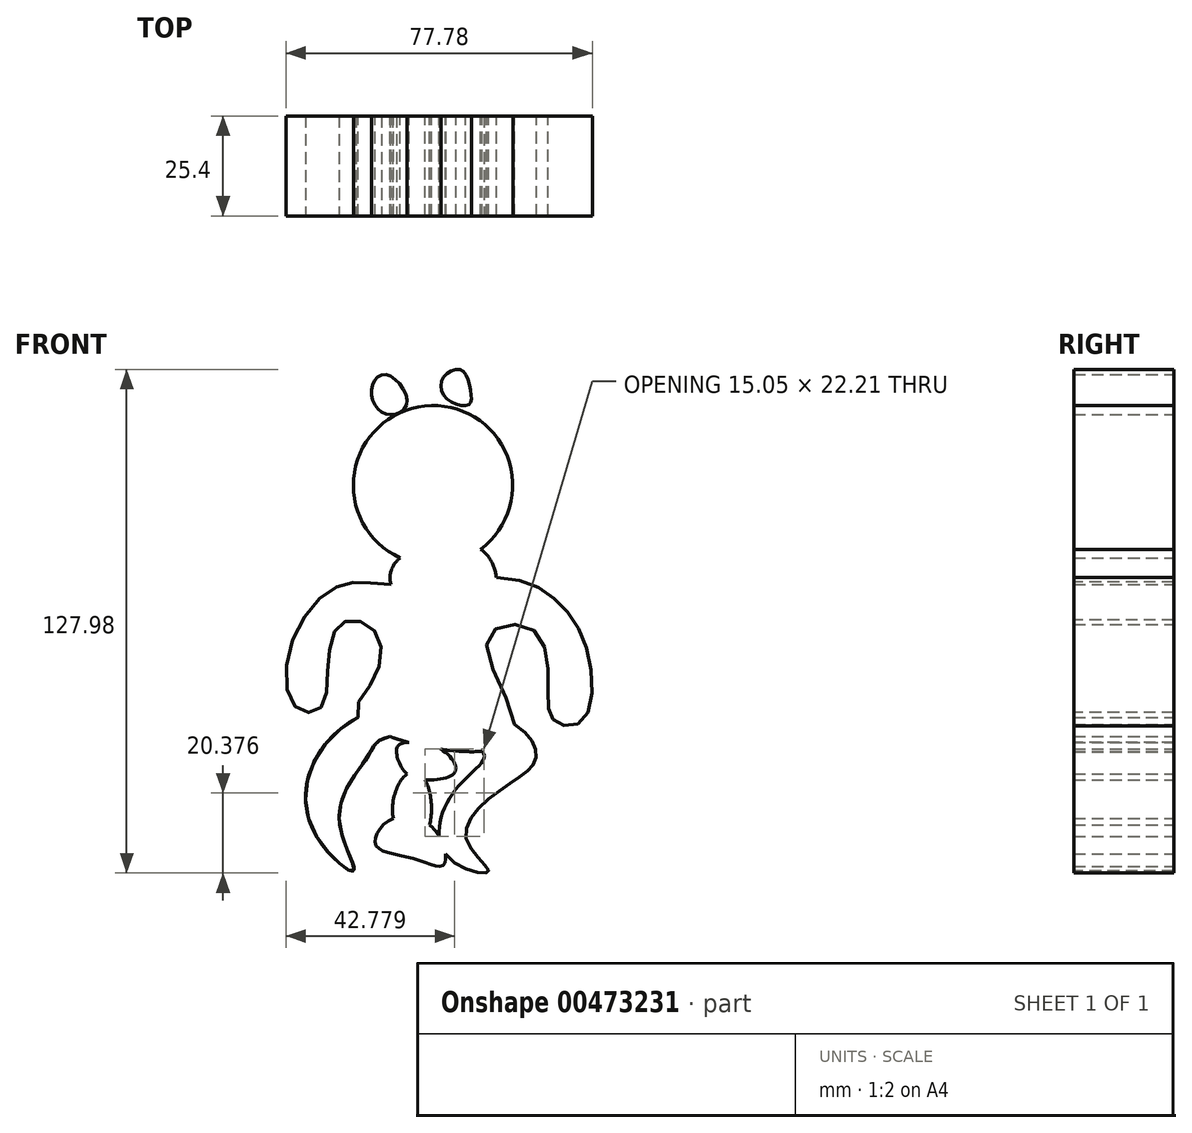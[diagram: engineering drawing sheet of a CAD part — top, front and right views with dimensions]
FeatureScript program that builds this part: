
annotation { "Feature Type Name" : "Feature", "Feature Type Description" : "" }
export const myFeature = defineFeature(function(context is Context, id is Id, definition is map)
    precondition{}
    {
        {
            var Q0;
            Q0=qCreatedBy(makeId("Front.planeOp"),FACE);
            var sketch = newSketch(context, id + "F0", { "sketchPlane" : qUnion([Q0])});
            skCircle(sketch, "E0", {"center": v(0, 25.17) * mm, "radius": 20.25 * mm});
            skSolve(sketch);
        }
        {
            var Q0;
            Q0 = qSketchRegion(id + "F0", true);
            extrude(context, id + "F1", {"entities" : qUnion([Q0]), "depth" : 25.4 * mm});
        }
        {
            var Q0;
            Q0=qCreatedBy(makeId("Front.planeOp"),FACE);
            var sketch = newSketch(context, id + "F2", { "sketchPlane" : qUnion([Q0])});
            skFitSpline(sketch, "E1", {"points": [v(-11.9, 43.27) * mm, v(-15.67, 49.13) * mm, v(-11.98, 53.29) * mm, v(-6.63, 46.06) * mm, v(-11.9, 43.27) * mm]});
            skSolve(sketch);
        }
        {
            var Q0;
            Q0 = qSketchRegion(id + "F2", true);
            extrude(context, id + "F3", {"entities" : qUnion([Q0]), "depth" : 25.4 * mm});
        }
        {
            var Q0;
            Q0=qCreatedBy(makeId("Front.planeOp"),FACE);
            var sketch = newSketch(context, id + "F4", { "sketchPlane" : qUnion([Q0])});
            skFitSpline(sketch, "E2", {"points": [v(3.54, 47.13) * mm, v(2.52, 52.42) * mm, v(7.2, 54.42) * mm, v(9.6, 48.75) * mm, v(9.04, 45.6) * mm, v(3.54, 47.13) * mm]});
            skSolve(sketch);
        }
        {
            var Q0;
            Q0 = qSketchRegion(id + "F4", true);
            extrude(context, id + "F5", {"entities" : qUnion([Q0]), "depth" : 25.4 * mm});
        }
        {
            var Q0;
            Q0=qCreatedBy(makeId("Front.planeOp"),FACE);
            var sketch = newSketch(context, id + "F6", { "sketchPlane" : qUnion([Q0])});
            skFitSpline(sketch, "E3", {"points": [v(-8.62, 6.56) * mm, v(-8.62, -3.04) * mm, v(13.51, -5.2) * mm, v(12.34, 8.72) * mm, v(-8.62, 6.56) * mm]});
            skSolve(sketch);
        }
        {
            var Q0;
            Q0 = qSketchRegion(id + "F6", true);
            extrude(context, id + "F7", {"entities" : qUnion([Q0]), "operationType" : NewBodyOperationType.ADD, "depth" : 25.4 * mm});
        }
        {
            var Q0;
            Q0=qCreatedBy(makeId("Front.planeOp"),FACE);
            var sketch = newSketch(context, id + "F8", { "sketchPlane" : qUnion([Q0])});
            skFitSpline(sketch, "E4", {"points": [v(-10.97, 0) * mm, v(-22.92, 0) * mm, v(-35.06, -12.63) * mm, v(-35.26, -30.85) * mm, v(-28.8, -31.63) * mm, v(-26.64, -19.3) * mm, v(-22.52, -9.5) * mm, v(-14.5, -12.24) * mm, v(-15.28, -24.38) * mm, v(-18.6, -34.37) * mm, v(19.98, -39.66) * mm, v(13.71, -14.2) * mm, v(25.46, -11.65) * mm, v(29.18, -28.1) * mm, v(31.14, -34.96) * mm, v(37.8, -34.77) * mm, v(39.76, -19.3) * mm, v(32.12, -4.8) * mm, v(17.63, 1.66) * mm, v(-10.97, 0) * mm]});
            skSolve(sketch);
        }
        {
            var Q0;
            Q0 = qSketchRegion(id + "F8", true);
            extrude(context, id + "F9", {"entities" : qUnion([Q0]), "operationType" : NewBodyOperationType.ADD, "depth" : 25.4 * mm});
        }
        {
            var Q0;
            Q0=qCreatedBy(makeId("Front.planeOp"),FACE);
            var sketch = newSketch(context, id + "F10", { "sketchPlane" : qUnion([Q0])});
            skFitSpline(sketch, "E5", {"points": [v(-19.4, -33.98) * mm, v(-31.34, -60.42) * mm, v(-20.17, -72.76) * mm, v(-23.9, -59.25) * mm, v(-16.45, -43.58) * mm, v(-11.75, -38.88) * mm, v(12.73, -42.8) * mm, v(5.68, -52.2) * mm, v(3.72, -69.24) * mm, v(14.1, -72.96) * mm, v(8.42, -64.73) * mm, v(17.43, -52) * mm, v(26.05, -44.56) * mm, v(20.37, -35.35) * mm, v(-19.4, -33.98) * mm]});
            skSolve(sketch);
        }
        {
            var Q0;
            Q0 = qSketchRegion(id + "F10", true);
            extrude(context, id + "F11", {"entities" : qUnion([Q0]), "operationType" : NewBodyOperationType.ADD, "depth" : 25.4 * mm});
        }
        {
            var Q0;
            Q0=qCreatedBy(makeId("Front.planeOp"),FACE);
            var sketch = newSketch(context, id + "F12", { "sketchPlane" : qUnion([Q0])});
            skFitSpline(sketch, "E6", {"points": [v(-5.1, -40.25) * mm, v(-9, -41.23) * mm, v(-7.25, -47.5) * mm, v(0, -49.65) * mm, v(5.68, -47.5) * mm, v(2.74, -42.4) * mm, v(-5.1, -40.25) * mm]});
            skSolve(sketch);
        }
        {
            var Q0;
            Q0 = qSketchRegion(id + "F12", true);
            extrude(context, id + "F13", {"entities" : qUnion([Q0]), "operationType" : NewBodyOperationType.ADD, "depth" : 25.4 * mm});
        }
        {
            var Q0;
            Q0=qCreatedBy(makeId("Front.planeOp"),FACE);
            var sketch = newSketch(context, id + "F14", { "sketchPlane" : qUnion([Q0])});
            skFitSpline(sketch, "E7", {"points": [v(-6.46, -48.08) * mm, v(-9.8, -60.23) * mm, v(-2.55, -63.75) * mm, v(-1.76, -50.24) * mm, v(-6.46, -48.08) * mm]});
            skSolve(sketch);
        }
        {
            var Q0;
            Q0=makeQuery(id+"F14.imprint","IMPRINT",FACE,{"disambiguationData":[TD([[makeQuery(id+"F14.imprint","IMPRINT",EDGE,{"derivedFrom":sQuery(id+"F14.wireOp",EDGE,"E7")}),1.0]])]});
            extrude(context, id + "F15", {"entities" : qUnion([Q0]), "operationType" : NewBodyOperationType.ADD, "depth" : 25.4 * mm});
        }
        {
            var Q0;
            Q0=qCreatedBy(makeId("Front.planeOp"),FACE);
            var sketch = newSketch(context, id + "F16", { "sketchPlane" : qUnion([Q0])});
            skFitSpline(sketch, "E8", {"points": [v(-11.16, -60.03) * mm, v(-14.5, -66.3) * mm, v(-5.1, -69.63) * mm, v(2.74, -71.2) * mm, v(0, -62) * mm, v(-11.16, -60.03) * mm]});
            skSolve(sketch);
        }
        {
            var Q0;
            Q0 = qSketchRegion(id + "F16", true);
            extrude(context, id + "F17", {"entities" : qUnion([Q0]), "operationType" : NewBodyOperationType.ADD, "depth" : 25.4 * mm});
        }
    });
